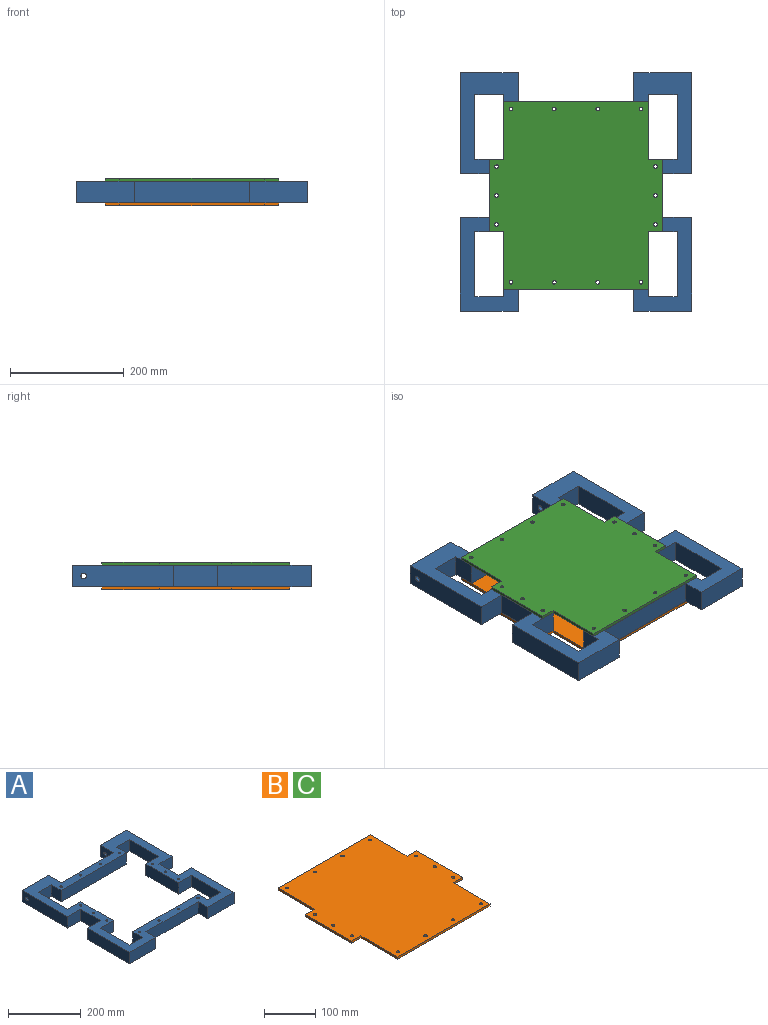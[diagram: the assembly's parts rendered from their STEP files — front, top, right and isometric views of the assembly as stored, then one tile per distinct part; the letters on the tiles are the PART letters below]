
ASSEMBLY  parts=3 mates=4
PART A: 58 faces, bbox 406.4x419.1x38.1 mm
  f0: plane 114.3x38.1mm, normal (-1,0,0), area 4354.8mm2, adj f1,f39,f40,f41
  f1: plane 50.8x38.1mm, normal (0,1,0), area 1935.5mm2, adj f0,f2,f40,f41
  f2: plane 127x38.1mm, normal (-1,0,0), area 4838.7mm2, adj f1,f3,f40,f41
  f3: plane 50.8x38.1mm, normal (0,-1,0), area 1935.5mm2, adj f2,f4,f40,f41
  f4: plane 114.3x38.1mm, normal (-1,0,0), area 4354.8mm2, adj f3,f5,f40,f41
  f5: plane 50.8x38.1mm, normal (0,1,0), area 1935.5mm2, adj f4,f6,f40,f41
  f6: plane 38.1x38.1mm, normal (1,0,0), area 1451.6mm2, adj f5,f7,f40,f41
  f7: plane 254x38.1mm, normal (0,1,0), area 9677.4mm2, adj f6,f8,f40,f41
  f8: plane 38.1x38.1mm, normal (-1,0,0), area 1451.6mm2, adj f7,f9,f40,f41
  f9: plane 50.8x38.1mm, normal (0,1,0), area 1935.5mm2, adj f8,f10,f40,f41
  f10: plane 114.3x38.1mm, normal (1,0,0), area 4354.8mm2, adj f9,f11,f40,f41
  f11: plane 50.8x38.1mm, normal (0,-1,0), area 1935.5mm2, adj f10,f12,f40,f41
  f12: plane 127x38.1mm, normal (1,0,0), area 4838.7mm2, adj f11,f13,f40,f41
  f13: plane 50.8x38.1mm, normal (0,1,0), area 1935.5mm2, adj f12,f14,f40,f41
  f14: plane 114.3x38.1mm, normal (1,0,0), area 4354.8mm2, adj f13,f15,f40,f41
  f15: plane 50.8x38.1mm, normal (0,-1,0), area 1935.5mm2, adj f14,f16,f40,f41
  f16: plane 38.1x38.1mm, normal (-1,0,0), area 1451.6mm2, adj f15,f17,f40,f41
  f17: plane 254x38.1mm, normal (0,-1,0), area 9677.4mm2, adj f16,f18,f40,f41
  f18: plane 38.1x38.1mm, normal (1,0,0), area 1451.6mm2, adj f17,f39,f40,f41
  f19: plane 165.1x38.1mm, normal (-1,0,0), area 6290.3mm2, adj f20,f38,f40,f41
  f20: plane 101.6x38.1mm, normal (0,-1,0), area 3871mm2, adj f19,f21,f40,f41
  f21: plane 38.1x38.1mm, normal (1,0,0), area 1451.6mm2, adj f20,f22,f40,f41
  f22: plane 203.2x38.1mm, normal (0,-1,0), area 7741.9mm2, adj f21,f23,f40,f41
  f23: plane 38.1x38.1mm, normal (-1,0,0), area 1451.6mm2, adj f22,f24,f40,f41
  f24: plane 101.6x38.1mm, normal (0,-1,0), area 3871mm2, adj f23,f25,f40,f41
  f25: plane 165.1x38.1mm, normal (1,0,0), area 6290.3mm2, adj f24,f26,f40,f41
  f26: plane 50.8x38.1mm, normal (0,1,0), area 1935.5mm2, adj f25,f27,f40,f41
  f27: plane 76.2x38.1mm, normal (1,0,0), area 2903.2mm2, adj f26,f28,f40,f41
  f28: plane 50.8x38.1mm, normal (0,-1,0), area 1935.5mm2, adj f27,f29,f40,f41
  f29: plane 177.8x38.1mm, normal (1,0,0), area 6702.9mm2, adj f28,f30,f40,f41,f43
  f30: plane 101.6x38.1mm, normal (0,1,0), area 3871mm2, adj f29,f31,f40,f41
  f31: plane 50.8x38.1mm, normal (-1,0,0), area 1864.2mm2, adj f30,f32,f40,f41,f43
  f32: plane 203.2x38.1mm, normal (0,1,0), area 7741.9mm2, adj f31,f33,f40,f41
  f33: plane 50.8x38.1mm, normal (1,0,0), area 1864.2mm2, adj f32,f34,f40,f41,f42
  f34: plane 101.6x38.1mm, normal (0,1,0), area 3871mm2, adj f33,f35,f40,f41
  f35: plane 177.8x38.1mm, normal (-1,0,0), area 6702.9mm2, adj f34,f36,f40,f41,f42
  f36: plane 50.8x38.1mm, normal (0,-1,0), area 1935.5mm2, adj f35,f37,f40,f41
  f37: plane 76.2x38.1mm, normal (-1,0,0), area 2903.2mm2, adj f36,f38,f40,f41
  f38: plane 50.8x38.1mm, normal (0,1,0), area 1935.5mm2, adj f19,f37,f40,f41
  f39: plane 50.8x38.1mm, normal (0,-1,0), area 1935.5mm2, adj f0,f18,f40,f41
  f40: plane 419.1x406.4mm, normal (0,0,1), area 49879.1mm2, adj f0,f1,f2,f3,f4,f5,f6,f7
  f41: plane 419.1x406.4mm, normal (0,0,-1), area 49879.1mm2, adj f0,f1,f2,f3,f4,f5,f6,f7
  f42: cylinder r=4.76mm len=101.6mm, axis (1,0,0), area 3040.2mm2, adj f33,f35
  f43: cylinder r=4.76mm len=101.6mm, axis (1,0,0), area 3040.2mm2, adj f29,f31
  f44: cylinder r=3.17mm len=38.1mm, axis (0,0,1), area 760.1mm2, adj f40,f41
  f45: cylinder r=3.17mm len=38.1mm, axis (0,0,1), area 760.1mm2, adj f40,f41
  f46: cylinder r=3.17mm len=38.1mm, axis (0,0,1), area 760.1mm2, adj f40,f41
  f47: cylinder r=3.17mm len=38.1mm, axis (0,0,1), area 760.1mm2, adj f40,f41
  f48: cylinder r=3.17mm len=38.1mm, axis (0,0,1), area 760.1mm2, adj f40,f41
  f49: cylinder r=3.17mm len=38.1mm, axis (0,0,1), area 760.1mm2, adj f40,f41
  f50: cylinder r=3.17mm len=38.1mm, axis (0,0,1), area 760.1mm2, adj f40,f41
  f51: cylinder r=3.17mm len=38.1mm, axis (0,0,1), area 760.1mm2, adj f40,f41
  f52: cylinder r=3.17mm len=38.1mm, axis (0,0,1), area 760.1mm2, adj f40,f41
  f53: cylinder r=3.17mm len=38.1mm, axis (0,0,1), area 760.1mm2, adj f40,f41
  f54: cylinder r=3.17mm len=38.1mm, axis (0,0,1), area 760.1mm2, adj f40,f41
  f55: cylinder r=3.17mm len=38.1mm, axis (0,0,1), area 760.1mm2, adj f40,f41
  f56: cylinder r=3.17mm len=38.1mm, axis (0,0,1), area 760.1mm2, adj f40,f41
  f57: cylinder r=3.17mm len=38.1mm, axis (0,0,1), area 760.1mm2, adj f40,f41
PART B: 28 faces, bbox 304.8x330.2x5.1 mm
  f0: plane 101.6x5.08mm, normal (-1,0,0), area 516.1mm2, adj f1,f11,f12,f13
  f1: plane 25.4x5.08mm, normal (0,1,0), area 129mm2, adj f0,f2,f12,f13
  f2: plane 127x5.08mm, normal (-1,0,0), area 645.2mm2, adj f1,f3,f12,f13
  f3: plane 25.4x5.08mm, normal (0,-1,0), area 129mm2, adj f2,f4,f12,f13
  f4: plane 101.6x5.08mm, normal (-1,0,0), area 516.1mm2, adj f3,f5,f12,f13
  f5: plane 254x5.08mm, normal (0,-1,0), area 1290.3mm2, adj f4,f6,f12,f13
  f6: plane 101.6x5.08mm, normal (1,0,0), area 516.1mm2, adj f5,f7,f12,f13
  f7: plane 25.4x5.08mm, normal (0,-1,0), area 129mm2, adj f6,f8,f12,f13
  f8: plane 127x5.08mm, normal (1,0,0), area 645.2mm2, adj f7,f9,f12,f13
  f9: plane 25.4x5.08mm, normal (0,1,0), area 129mm2, adj f8,f10,f12,f13
  f10: plane 101.6x5.08mm, normal (1,0,0), area 516.1mm2, adj f9,f11,f12,f13
  f11: plane 254x5.08mm, normal (0,1,0), area 1290.3mm2, adj f0,f10,f12,f13
  f12: plane 330.2x304.8mm, normal (0,0,1), area 89879mm2, adj f0,f1,f2,f3,f4,f5,f6,f7
  f13: plane 330.2x304.8mm, normal (0,0,-1), area 89879mm2, adj f0,f1,f2,f3,f4,f5,f6,f7
  f14: cylinder r=3.17mm len=6.35mm, axis (0,0,1), area 101.3mm2, adj f12,f13
  f15: cylinder r=3.17mm len=6.35mm, axis (0,0,1), area 101.3mm2, adj f12,f13
  f16: cylinder r=3.17mm len=6.35mm, axis (0,0,1), area 101.3mm2, adj f12,f13
  f17: cylinder r=3.17mm len=6.35mm, axis (0,0,1), area 101.3mm2, adj f12,f13
  f18: cylinder r=3.17mm len=6.35mm, axis (0,0,1), area 101.3mm2, adj f12,f13
  f19: cylinder r=3.17mm len=6.35mm, axis (0,0,1), area 101.3mm2, adj f12,f13
  f20: cylinder r=3.17mm len=6.35mm, axis (0,0,1), area 101.3mm2, adj f12,f13
  f21: cylinder r=3.17mm len=6.35mm, axis (0,0,1), area 101.3mm2, adj f12,f13
  f22: cylinder r=3.17mm len=6.35mm, axis (0,0,1), area 101.3mm2, adj f12,f13
  f23: cylinder r=3.17mm len=6.35mm, axis (0,0,1), area 101.3mm2, adj f12,f13
  f24: cylinder r=3.17mm len=6.35mm, axis (0,0,1), area 101.3mm2, adj f12,f13
  f25: cylinder r=3.17mm len=6.35mm, axis (0,0,1), area 101.3mm2, adj f12,f13
  f26: cylinder r=3.17mm len=6.35mm, axis (0,0,1), area 101.3mm2, adj f12,f13
  f27: cylinder r=3.17mm len=6.35mm, axis (0,0,1), area 101.3mm2, adj f12,f13
PART C: same geometry as B
PLACE A t=(5.37,-60.46,-14.35)mm
PLACE B t=(5.37,-60.46,-19.43)mm
PLACE C t=(5.37,-60.46,23.75)mm
MATE cylindrical A.f52 <-> C.f22  axis (0,0,1) through (145.07,-250.96,23.75)mm
MATE planar B.f12 <-> A.f41  axis (0,0,1) through (5.37,-200.16,-14.35)mm
MATE planar C.f26 <-> A.f40  axis (0,0,-1) through (43.47,-47.76,23.75)mm
MATE cylindrical C.f22 <-> B.f22  axis (0,0,1) through (145.07,-250.96,28.83)mm
